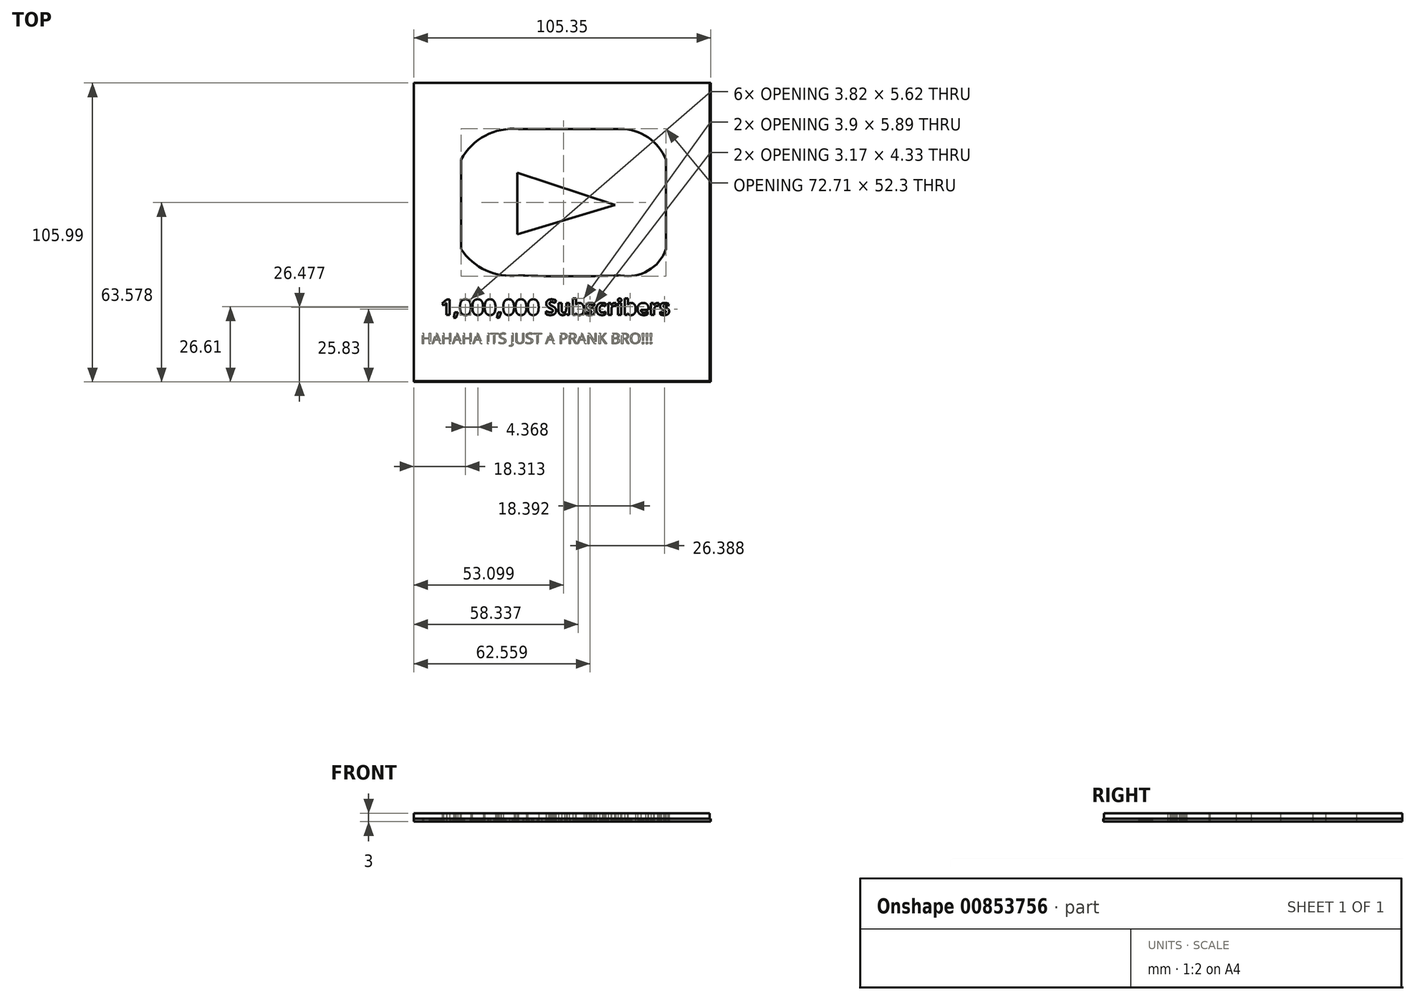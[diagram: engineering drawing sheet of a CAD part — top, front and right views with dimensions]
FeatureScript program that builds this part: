
annotation { "Feature Type Name" : "Feature", "Feature Type Description" : "" }
export const myFeature = defineFeature(function(context is Context, id is Id, definition is map)
    precondition{}
    {
        {
            var Q0;
            Q0=qCreatedBy(makeId("Top.planeOp"),FACE);
            var sketch = newSketch(context, id + "F0", { "sketchPlane" : qUnion([Q0])});
            skArc(sketch, "E0", {"start": v(-24.7, 42.6) * mm, "mid": v(-36.49, 40.25) * mm, "end": v(-45.05, 31.8) * mm});
            skLineSegment(sketch, "E1", {"start": v(-45.05, 31.8) * mm, "end": v(-45.05, 0) * mm});
            skArc(sketch, "E2", {"start": v(-45.05, 0) * mm, "mid": v(-36.18, -7.53) * mm, "end": v(-24.7, -9.33) * mm});
            skLineSegment(sketch, "E3", {"start": v(-24.7, 42.6) * mm, "end": v(11.55, 42.6) * mm});
            skArc(sketch, "E4", {"start": v(27.66, 31.8) * mm, "mid": v(21.25, 39.65) * mm, "end": v(11.55, 42.6) * mm});
            skLineSegment(sketch, "E5", {"start": v(27.66, 31.8) * mm, "end": v(27.66, 0) * mm});
            skArc(sketch, "E6", {"start": v(11.55, -9.33) * mm, "mid": v(21.31, -7.6) * mm, "end": v(27.66, 0) * mm});
            skArc(sketch, "E7", {"start": v(-24.7, -9.33) * mm, "mid": v(-6.57, -9.63) * mm, "end": v(11.55, -9.33) * mm});
            skLineSegment(sketch, "E8", {"start": v(-23.64, 32) * mm, "end": v(-23.64, 0) * mm});
            skLineSegment(sketch, "E9", {"start": v(-23.64, 0) * mm, "end": v(13.46, 14) * mm});
            skLineSegment(sketch, "E10", {"start": v(13.46, 14) * mm, "end": v(-23.64, 32) * mm});
            skLineSegment(sketch, "E11", {"start": v(-61.8, 58.93) * mm, "end": v(-61.8, -46.85) * mm});
            skLineSegment(sketch, "E12", {"start": v(-61.8, -46.85) * mm, "end": v(43.14, -46.85) * mm});
            skLineSegment(sketch, "E13", {"start": v(43.14, -46.85) * mm, "end": v(43.14, 58.93) * mm});
            skLineSegment(sketch, "E14", {"start": v(43.14, 58.93) * mm, "end": v(-61.8, 58.93) * mm});
            skText(sketch, "E15", { "text": "1,000,000 Subscribers", "fontName": "OpenSans-Bold.ttf"});
            const initialGuessF0  = {"E15": [-0.05225, -0.02332, 1, 0, 0.00551]};
            skSetInitialGuess(sketch, initialGuessF0);
            skSolve(sketch);
        }
        {
            var Q0;
            Q0=makeQuery(id+"F0.imprint","IMPRINT",FACE,{"disambiguationData":[TD([[makeQuery(id+"F0.imprint","IMPRINT",EDGE,{"derivedFrom":sQuery(id+"F0.wireOp",EDGE,"E0")}),-1.0]])]});
            extrude(context, id + "F1", {"entities" : qUnion([Q0]), "depth" : 3 * mm, "offsetDistance" : 25 * mm});
        }
        {
            var Q0;
            Q0=qCreatedBy(makeId("Top.planeOp"),FACE);
            var sketch = newSketch(context, id + "F2", { "sketchPlane" : qUnion([Q0])});
            skLineSegment(sketch, "E16", {"start": v(-25.12, 27.13) * mm, "end": v(-25.12, 5.3) * mm});
            skLineSegment(sketch, "E17", {"start": v(-25.12, 5.3) * mm, "end": v(9.65, 15.69) * mm});
            skLineSegment(sketch, "E18", {"start": v(9.65, 15.69) * mm, "end": v(-25.12, 27.13) * mm});
            skSolve(sketch);
        }
        {
            var Q0;
            Q0 = qSketchRegion(id + "F2", true);
            extrude(context, id + "F3", {"entities" : qUnion([Q0]), "depth" : 3 * mm, "offsetDistance" : 25 * mm});
        }
        {
            var Q0;
            Q0=qCreatedBy(makeId("Top.planeOp"),FACE);
            var sketch = newSketch(context, id + "F4", { "sketchPlane" : qUnion([Q0])});
            skLineSegment(sketch, "E19.bottom", {"start": v(-61.8, -47.06) * mm, "end": v(43.56, -47.06) * mm});
            skLineSegment(sketch, "E19.top", {"start": v(-61.8, 58.93) * mm, "end": v(43.56, 58.93) * mm});
            skLineSegment(sketch, "E19.left", {"start": v(-61.8, -47.06) * mm, "end": v(-61.8, 58.93) * mm});
            skLineSegment(sketch, "E19.right", {"start": v(43.56, -47.06) * mm, "end": v(43.56, 58.93) * mm});
            skSolve(sketch);
        }
        {
            var Q0;
            Q0 = qSketchRegion(id + "F4", true);
            extrude(context, id + "F5", {"entities" : qUnion([Q0]), "depth" : 1 * mm, "offsetDistance" : 25 * mm});
        }
        {
            var Q0;
            Q0=qCreatedBy(makeId("Top.planeOp"),FACE);
            var sketch = newSketch(context, id + "F6", { "sketchPlane" : qUnion([Q0])});
            skText(sketch, "E20", { "text": "HAHAHA ITS JUST A PRANK BRO!!!", "fontName": "OpenSans-Regular.ttf"});
            const initialGuessF6  = {"E20": [-0.05925, -0.03354, 1, 0, 0.0038]};
            skSetInitialGuess(sketch, initialGuessF6);
            skSolve(sketch);
        }
        {
            var Q0;
            Q0 = qSketchRegion(id + "F6", true);
            extrude(context, id + "F7", {"entities" : qUnion([Q0]), "depth" : 1 * mm, "offsetDistance" : 25 * mm});
        }
    });
